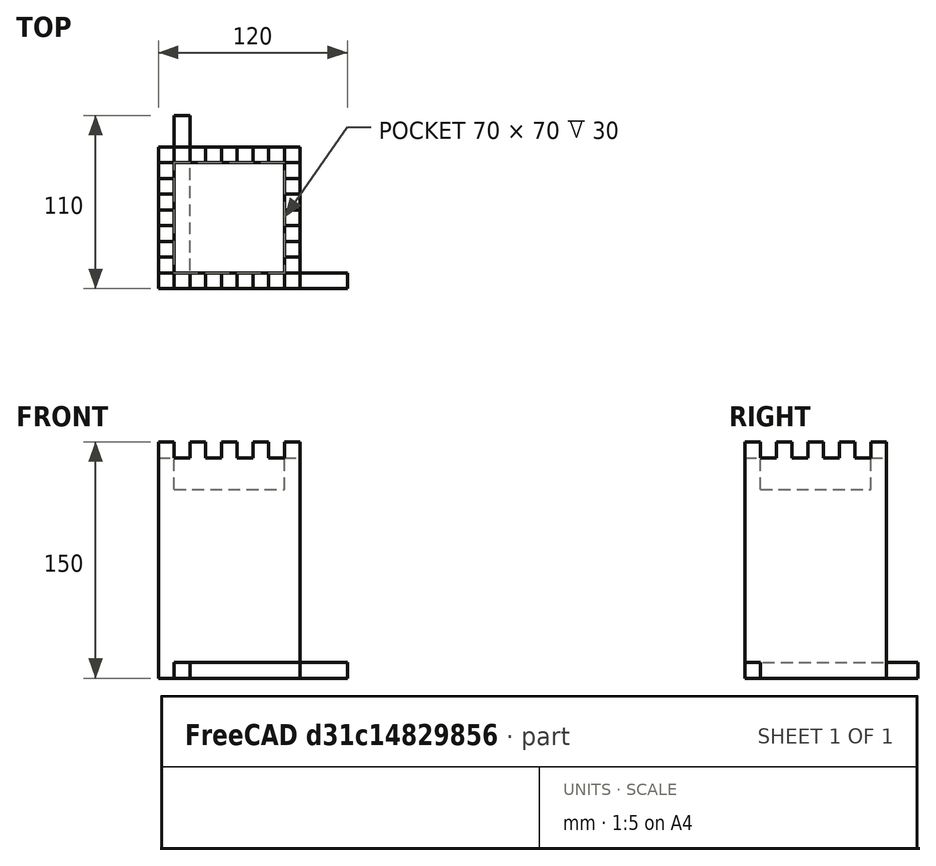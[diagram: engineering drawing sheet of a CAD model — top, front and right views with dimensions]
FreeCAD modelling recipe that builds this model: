
FCSTD DOCUMENT  (FreeCAD 1.0R39319 (Git))
Label: ojt1_t10r02_tower
License: All rights reserved
LicenseURL: https://en.wikipedia.org/wiki/All_rights_reserved
objects: Part::Box×4, Part::FeaturePython×2, Part::Cut×2, Part::Fuse×1
note: 7 computed .brp shape members not serialized (recipe doc carries the construction recipe); baked Part::Feature solids carry a one-line shape summary decoded from their .brp

FEATURE [Part::Box] Box  label="Cub"
  AttacherType = Attacher::AttachEngine3D
  Height = 10
  Length = 10
  Width = 110
FEATURE [Part::FeaturePython] Array  # Draft array (typed FeaturePython)
  AlwaysSyncPlacement = false
  Angle = 360
  ArrayType = 0
  Axis = (0,0,1)
  Base = -> Box
  Center = (0,0,0)
  Count = 4
  ExpandArray = false
  Fuse = false
  IntervalAxis = (0,0,0)
  IntervalX = (20,0,0)
  IntervalY = (0,10,0)
  IntervalZ = (0,0,100)
  NumberCircles = 3
  NumberPolar = 5
  NumberX = 4
  NumberY = 0
  NumberZ = 1
  PlacementList = 4 placements: arithmetic series from (0,0,0) step (20,0,0) to (60,0,0)
  RadialDistance = 50
  ScaleList = (4) [(1,1,1),(1,1,1),(1,1,1),(1,1,1)]
  Symmetry = 1
  TangentialDistance = 25
FEATURE [Part::Box] Box001  label="Cub001"
  AttacherType = Attacher::AttachEngine3D
  Height = 10
  Length = 110
  Width = 10
FEATURE [Part::FeaturePython] Array001  # Draft array (typed FeaturePython)
  AlwaysSyncPlacement = false
  Angle = 360
  ArrayType = 0
  Axis = (0,0,1)
  Base = -> Box001
  Center = (0,0,0)
  Count = 4
  ExpandArray = false
  Fuse = false
  IntervalAxis = (0,0,0)
  IntervalX = (0,0,0)
  IntervalY = (0,20,0)
  IntervalZ = (0,0,100)
  NumberCircles = 3
  NumberPolar = 5
  NumberX = 1
  NumberY = 4
  NumberZ = 1
  Placement = pos=(-20,20,0) rot=(0,0,1;0rad)
  PlacementList = 4 placements: arithmetic series from (0,0,0) step (0,20,0) to (0,60,0)
  RadialDistance = 50
  ScaleList = (4) [(1,1,1),(1,1,1),(1,1,1),(1,1,1)]
  Symmetry = 1
  TangentialDistance = 25
FEATURE [Part::Fuse] Fusion
  Base = -> Array
  Placement = pos=(0,-10,140) rot=(0,0,1;0rad)
  Refine = true
  Tool = -> Array001
FEATURE [Part::Box] Box002  label="Cub002"
  AttacherType = Attacher::AttachEngine3D
  Height = 150
  Length = 90
  Placement = pos=(-10,0,0) rot=(0,0,1;0rad)
  Width = 90
FEATURE [Part::Cut] Cut
  Base = -> Box002
  Refine = true
  Tool = -> Fusion
FEATURE [Part::Box] Box003  label="Cub003"
  AttacherType = Attacher::AttachEngine3D
  Height = 30
  Length = 70
  Placement = pos=(0,10,120) rot=(0,0,1;0rad)
  Width = 70
FEATURE [Part::Cut] Cut001
  Base = -> Cut
  Refine = true
  Tool = -> Box003
